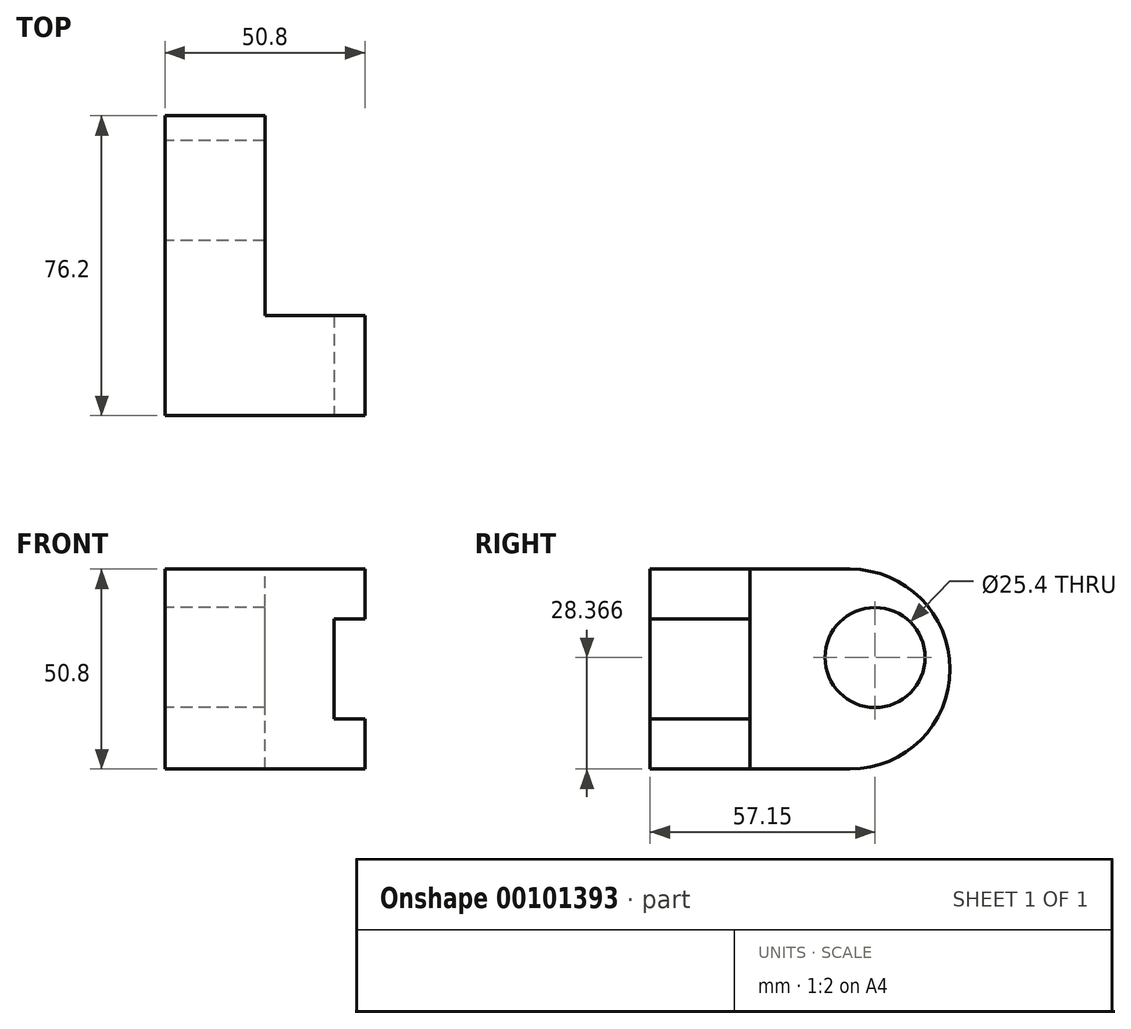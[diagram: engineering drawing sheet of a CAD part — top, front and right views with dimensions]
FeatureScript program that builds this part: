
annotation { "Feature Type Name" : "Feature", "Feature Type Description" : "" }
export const myFeature = defineFeature(function(context is Context, id is Id, definition is map)
    precondition{}
    {
        {
            var Q0;
            Q0=qCreatedBy(makeId("Front.planeOp"),FACE);
            var sketch = newSketch(context, id + "F0", { "sketchPlane" : qUnion([Q0])});
            skLineSegment(sketch, "E0", {"start": v(0, 0) * mm, "end": v(0, 50.8) * mm});
            skLineSegment(sketch, "E1", {"start": v(0, 50.8) * mm, "end": v(50.8, 50.8) * mm});
            skLineSegment(sketch, "E2", {"start": v(50.8, 50.8) * mm, "end": v(50.8, 38.1) * mm});
            skLineSegment(sketch, "E3", {"start": v(50.8, 38.1) * mm, "end": v(43, 38.1) * mm});
            skLineSegment(sketch, "E4", {"start": v(43, 38.1) * mm, "end": v(43, 12.7) * mm});
            skLineSegment(sketch, "E5", {"start": v(43, 12.7) * mm, "end": v(50.8, 12.7) * mm});
            skLineSegment(sketch, "E6", {"start": v(50.8, 12.7) * mm, "end": v(50.8, 0) * mm});
            skLineSegment(sketch, "E7", {"start": v(50.8, 0) * mm, "end": v(0, 0) * mm});
            skSolve(sketch);
        }
        {
            var Q0;
            Q0=qCreatedBy(makeId("Right.planeOp"),FACE);
            var sketch = newSketch(context, id + "F1", { "sketchPlane" : qUnion([Q0])});
            skLineSegment(sketch, "E8", {"start": v(0, 0) * mm, "end": v(50.8, 0) * mm});
            skLineSegment(sketch, "E9", {"start": v(76.2, 25.4) * mm, "end": v(76.2, 25.4) * mm});
            skLineSegment(sketch, "E10", {"start": v(50.8, 50.8) * mm, "end": v(0, 50.8) * mm});
            skLineSegment(sketch, "E11", {"start": v(0, 50.8) * mm, "end": v(0, 0) * mm});
            skCircle(sketch, "E12", {"center": v(57.15, 28.37) * mm, "radius": 12.7 * mm});
            skLineSegment(sketch, "E13", {"start": v(0, 0) * mm, "end": v(25.4, 0) * mm});
            skLineSegment(sketch, "E14", {"start": v(25.4, 0) * mm, "end": v(25.4, 50.8) * mm});
            skLineSegment(sketch, "E15", {"start": v(25.4, 50.8) * mm, "end": v(0, 50.8) * mm});
            skPoint(sketch, "E16.visualSharp", {"position": v(76.2, 50.8) * mm});
            skArc(sketch, "E16.filletArc", {"start": v(76.2, 25.4) * mm, "mid": v(68.76, 43.36) * mm, "end": v(50.8, 50.8) * mm});
            skPoint(sketch, "E17.visualSharp", {"position": v(76.2, 0) * mm});
            skArc(sketch, "E17.filletArc", {"start": v(50.8, 0) * mm, "mid": v(68.76, 7.44) * mm, "end": v(76.2, 25.4) * mm});
            skSolve(sketch);
        }
        {
            var Q0;
            Q0 = qSketchRegion(id + "F0", true);
            extrude(context, id + "F2", {"entities" : qUnion([Q0]), "oppositeDirection" : true, "depth" : 25.4 * mm});
        }
        {
            var Q0;
            Q0 = qSketchRegion(id + "F1", true);
            extrude(context, id + "F3", {"entities" : qUnion([Q0]), "operationType" : NewBodyOperationType.ADD, "depth" : 25.4 * mm});
        }
    });
